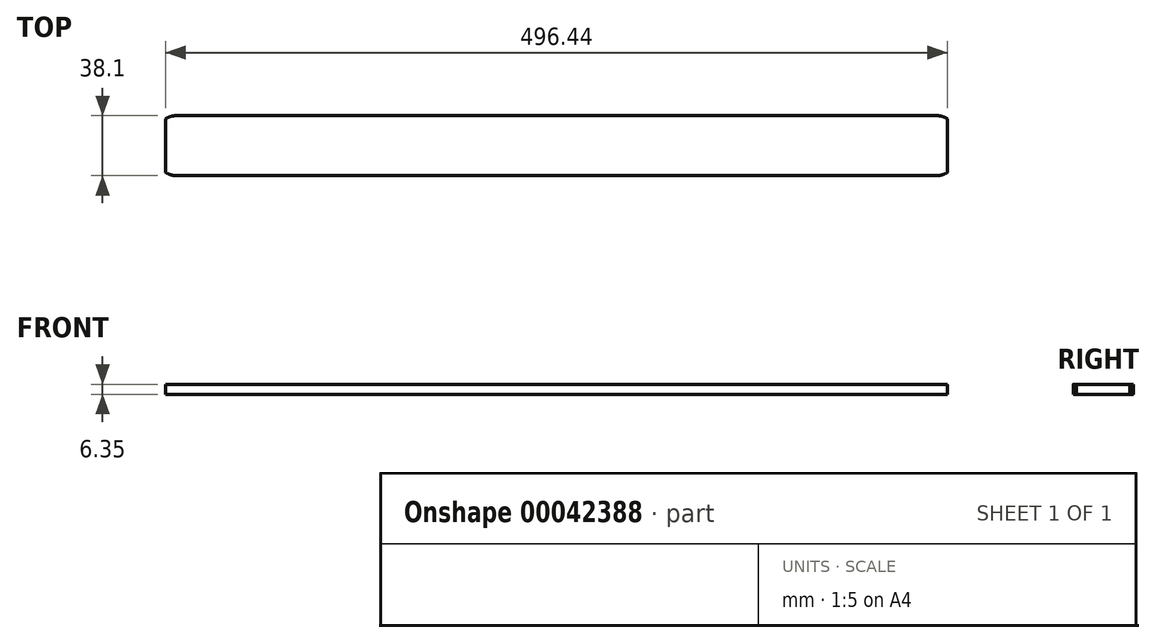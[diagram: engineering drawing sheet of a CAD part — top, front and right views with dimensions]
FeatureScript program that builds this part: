
annotation { "Feature Type Name" : "Feature", "Feature Type Description" : "" }
export const myFeature = defineFeature(function(context is Context, id is Id, definition is map)
    precondition{}
    {
        {
            var Q0;
            Q0=qCreatedBy(makeId("Top.planeOp"),FACE);
            var sketch = newSketch(context, id + "F0", { "sketchPlane" : qUnion([Q0])});
            skLineSegment(sketch, "E0.rect.bottom", {"start": v(-241.3, -19.05) * mm, "end": v(241.3, -19.05) * mm});
            skLineSegment(sketch, "E0.rect.top", {"start": v(-241.3, 19.05) * mm, "end": v(241.3, 19.05) * mm});
            skLineSegment(sketch, "E0.rect.left", {"start": v(-254, -6.35) * mm, "end": v(-254, 6.35) * mm});
            skLineSegment(sketch, "E0.rect.right", {"start": v(254, -6.35) * mm, "end": v(254, 6.35) * mm});
            skPoint(sketch, "E0.rect.middle", {"position": v(0, 0) * mm});
            skPoint(sketch, "E1.visualSharp", {"position": v(-254, 19.05) * mm});
            skArc(sketch, "E1.filletArc", {"start": v(-241.3, 19.05) * mm, "mid": v(-250.28, 15.33) * mm, "end": v(-254, 6.35) * mm});
            skPoint(sketch, "E2.visualSharp", {"position": v(-254, -19.05) * mm});
            skArc(sketch, "E2.filletArc", {"start": v(-254, -6.35) * mm, "mid": v(-250.28, -15.33) * mm, "end": v(-241.3, -19.05) * mm});
            skPoint(sketch, "E3.visualSharp", {"position": v(254, 19.05) * mm});
            skArc(sketch, "E3.filletArc", {"start": v(254, 6.35) * mm, "mid": v(250.28, 15.33) * mm, "end": v(241.3, 19.05) * mm});
            skPoint(sketch, "E4.visualSharp", {"position": v(254, -19.05) * mm});
            skArc(sketch, "E4.filletArc", {"start": v(241.3, -19.05) * mm, "mid": v(250.28, -15.33) * mm, "end": v(254, -6.35) * mm});
            skSolve(sketch);
        }
        {
            var Q0;
            Q0 = qSketchRegion(id + "F0", true);
            extrude(context, id + "F1", {"entities" : qUnion([Q0]), "depth" : 6.35 * mm});
        }
        {
            var Q0;
            Q0=makeQuery(id+"F1.opExtrude","CAP_FACE",FACE,{"disambiguationData":[OSD([sQuery(id+"F0.wireOp",EDGE,"E0.rect.bottom"),sQuery(id+"F0.wireOp",EDGE,"E0.rect.top"),sQuery(id+"F0.wireOp",EDGE,"E0.rect.left"),sQuery(id+"F0.wireOp",EDGE,"E0.rect.right"),sQuery(id+"F0.wireOp",EDGE,"E1.filletArc"),sQuery(id+"F0.wireOp",EDGE,"E2.filletArc"),sQuery(id+"F0.wireOp",EDGE,"E3.filletArc"),sQuery(id+"F0.wireOp",EDGE,"E4.filletArc")])],"isStart":false});
            var sketch = newSketch(context, id + "F2", { "sketchPlane" : qUnion([Q0])});
            skArc(sketch, "E5.0.0", {"start": v(-254, -6.35) * mm, "mid": v(-250.28, -15.33) * mm, "end": v(-241.3, -19.05) * mm});
            skLineSegment(sketch, "E5.0.1", {"start": v(-241.3, -19.05) * mm, "end": v(241.3, -19.05) * mm});
            skArc(sketch, "E5.0.2", {"start": v(241.3, -19.05) * mm, "mid": v(250.28, -15.33) * mm, "end": v(254, -6.35) * mm});
            skLineSegment(sketch, "E5.0.3", {"start": v(254, -6.35) * mm, "end": v(254, 6.35) * mm});
            skArc(sketch, "E5.0.4", {"start": v(254, 6.35) * mm, "mid": v(250.28, 15.33) * mm, "end": v(241.3, 19.05) * mm});
            skLineSegment(sketch, "E5.0.5", {"start": v(241.3, 19.05) * mm, "end": v(-241.3, 19.05) * mm});
            skArc(sketch, "E5.0.6", {"start": v(-241.3, 19.05) * mm, "mid": v(-250.28, 15.33) * mm, "end": v(-254, 6.35) * mm});
            skLineSegment(sketch, "E5.0.7", {"start": v(-254, 6.35) * mm, "end": v(-254, -6.35) * mm});
            skLineSegment(sketch, "E6", {"start": v(-250.28, 15.33) * mm, "end": v(-250.28, -15.33) * mm});
            skLineSegment(sketch, "E7", {"start": v(250.28, 15.33) * mm, "end": v(250.28, -15.33) * mm});
            skSolve(sketch);
        }
        {
            var Q0;
            {var subQ2=sQuery(id+"F2.wireOp",EDGE,"E5.0.3");Q0=makeQuery(id+"F2.imprint","IMPRINT",FACE,{"disambiguationData":[TD([[makeQuery(id+"F2.imprint","IMPRINT",EDGE,{"derivedFrom":subQ2}),1.0]])]});}
            var Q1;
            {var subQ1=sQuery(id+"F2.wireOp",EDGE,"E5.0.7");Q1=makeQuery(id+"F2.imprint","IMPRINT",FACE,{"disambiguationData":[TD([[makeQuery(id+"F2.imprint","IMPRINT",EDGE,{"derivedFrom":subQ1}),-1.0]])]});}
            extrude(context, id + "F3", {"entities" : qUnion([Q0, Q1]), "operationType" : NewBodyOperationType.REMOVE, "oppositeDirection" : true, "depth" : 25.4 * mm});
        }
        {
            var Q0;
            Q0=makeQuery(id+"F1.opExtrude","CAP_FACE",FACE,{"disambiguationData":[OSD([sQuery(id+"F0.wireOp",EDGE,"E0.rect.bottom"),sQuery(id+"F0.wireOp",EDGE,"E0.rect.top"),sQuery(id+"F0.wireOp",EDGE,"E0.rect.left"),sQuery(id+"F0.wireOp",EDGE,"E0.rect.right"),sQuery(id+"F0.wireOp",EDGE,"E1.filletArc"),sQuery(id+"F0.wireOp",EDGE,"E2.filletArc"),sQuery(id+"F0.wireOp",EDGE,"E3.filletArc"),sQuery(id+"F0.wireOp",EDGE,"E4.filletArc")])],"isStart":false});
            var sketch = newSketch(context, id + "F4", { "sketchPlane" : qUnion([Q0])});
            skLineSegment(sketch, "E8.rect.bottom", {"start": v(-248.22, 19.05) * mm, "end": v(248.22, 19.05) * mm});
            skLineSegment(sketch, "E8.rect.top", {"start": v(-248.22, -19.05) * mm, "end": v(248.22, -19.05) * mm});
            skLineSegment(sketch, "E8.rect.left", {"start": v(-248.22, 19.05) * mm, "end": v(-248.22, -19.05) * mm});
            skLineSegment(sketch, "E8.rect.right", {"start": v(248.22, 19.05) * mm, "end": v(248.22, -19.05) * mm});
            skPoint(sketch, "E8.rect.middle", {"position": v(0, 0) * mm});
            skLineSegment(sketch, "E9.0.0", {"start": v(250.28, -15.33) * mm, "end": v(250.28, 15.33) * mm});
            skArc(sketch, "E9.0.1", {"start": v(250.28, 15.33) * mm, "mid": v(246.16, 18.08) * mm, "end": v(241.3, 19.05) * mm});
            skLineSegment(sketch, "E9.0.2", {"start": v(241.3, 19.05) * mm, "end": v(-241.3, 19.05) * mm});
            skArc(sketch, "E9.0.3", {"start": v(-241.3, 19.05) * mm, "mid": v(-246.16, 18.08) * mm, "end": v(-250.28, 15.33) * mm});
            skLineSegment(sketch, "E9.0.4", {"start": v(-250.28, 15.33) * mm, "end": v(-250.28, -15.33) * mm});
            skArc(sketch, "E9.0.5", {"start": v(-250.28, -15.33) * mm, "mid": v(-246.16, -18.08) * mm, "end": v(-241.3, -19.05) * mm});
            skLineSegment(sketch, "E9.0.6", {"start": v(-241.3, -19.05) * mm, "end": v(241.3, -19.05) * mm});
            skArc(sketch, "E9.0.7", {"start": v(241.3, -19.05) * mm, "mid": v(246.16, -18.08) * mm, "end": v(250.28, -15.33) * mm});
            skSolve(sketch);
        }
        {
            var Q0;
            {var subQ3=sQuery(id+"F4.wireOp",EDGE,"E9.0.4");Q0=makeQuery(id+"F4.imprint","IMPRINT",FACE,{"disambiguationData":[TD([[makeQuery(id+"F4.imprint","IMPRINT",EDGE,{"derivedFrom":subQ3}),1.0]])]});}
            var Q1;
            {var subQ3=sQuery(id+"F4.wireOp",EDGE,"E9.0.0");Q1=makeQuery(id+"F4.imprint","IMPRINT",FACE,{"disambiguationData":[TD([[makeQuery(id+"F4.imprint","IMPRINT",EDGE,{"derivedFrom":subQ3}),-1.0]])]});}
            extrude(context, id + "F5", {"entities" : qUnion([Q0, Q1]), "operationType" : NewBodyOperationType.REMOVE, "oppositeDirection" : true, "depth" : 25.4 * mm});
        }
    });
